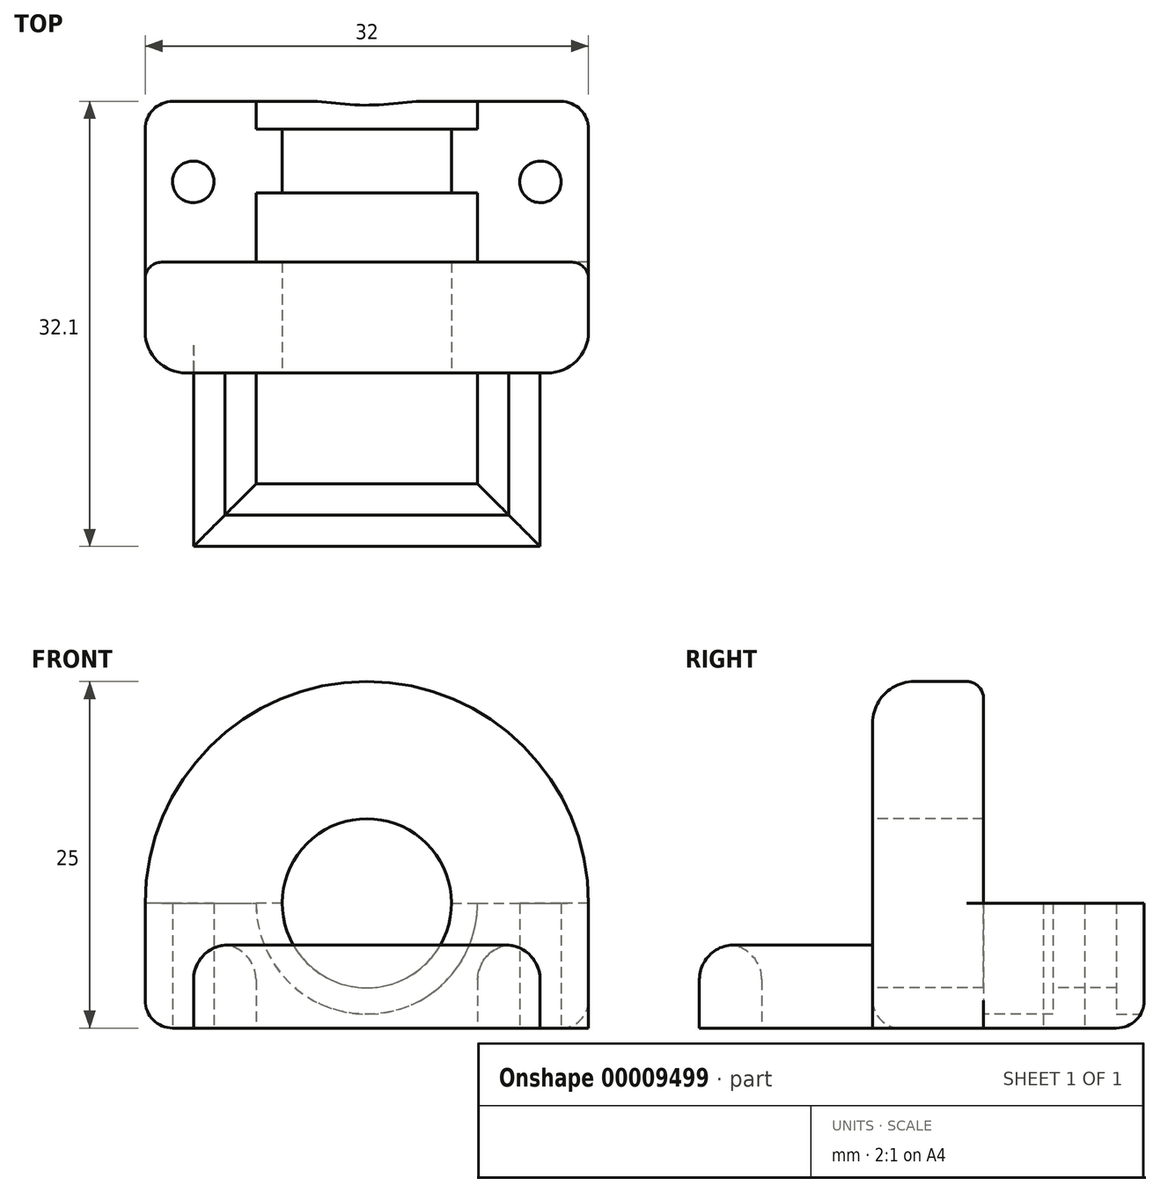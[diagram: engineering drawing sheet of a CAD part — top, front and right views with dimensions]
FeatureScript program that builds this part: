
annotation { "Feature Type Name" : "Feature", "Feature Type Description" : "" }
export const myFeature = defineFeature(function(context is Context, id is Id, definition is map)
    precondition{}
    {
        {
            var Q0;
            Q0=qCreatedBy(makeId("Top.planeOp"),FACE);
            var sketch = newSketch(context, id + "F0", { "sketchPlane" : qUnion([Q0])});
            skLineSegment(sketch, "E0.rect.bottom", {"start": v(-16, 5.8) * mm, "end": v(16, 5.8) * mm});
            skLineSegment(sketch, "E0.rect.top", {"start": v(-16, -5.8) * mm, "end": v(16, -5.8) * mm});
            skLineSegment(sketch, "E0.rect.left", {"start": v(-16, 5.8) * mm, "end": v(-16, -5.8) * mm});
            skLineSegment(sketch, "E0.rect.right", {"start": v(16, 5.8) * mm, "end": v(16, -5.8) * mm});
            skPoint(sketch, "E0.rect.middle", {"position": v(0, 0) * mm});
            skCircle(sketch, "E1", {"center": v(12.52, 0) * mm, "radius": 1.5 * mm});
            skCircle(sketch, "E2", {"center": v(-12.52, 0) * mm, "radius": 1.5 * mm});
            skSolve(sketch);
        }
        {
            var Q0;
            Q0=makeQuery(id+"F0.imprint","IMPRINT",FACE,{"disambiguationData":[TD([[makeQuery(id+"F0.imprint","IMPRINT",EDGE,{"derivedFrom":sQuery(id+"F0.wireOp",EDGE,"E0.rect.bottom")}),-1.0]])]});
            extrude(context, id + "F1", {"entities" : qUnion([Q0]), "depth" : 9 * mm});
        }
        {
            var Q0;
            Q0=makeQuery(id+"F1.opExtrude","SWEPT_FACE",FACE,{"disambiguationData":[OSD([sQuery(id+"F0.wireOp",EDGE,"E0.rect.top")])]});
            var sketch = newSketch(context, id + "F2", { "sketchPlane" : qUnion([Q0])});
            skCircle(sketch, "E3", {"center": v(0, 9) * mm, "radius": 8 * mm});
            skSolve(sketch);
        }
        {
            var Q0;
            Q0 = qSketchRegion(id + "F2", true);
            var Q1;
            Q1=makeQuery(id+"F1.opExtrude","SWEPT_FACE",FACE,{"disambiguationData":[OSD([sQuery(id+"F0.wireOp",EDGE,"E0.rect.bottom")])]});
            extrude(context, id + "F3", {"entities" : qUnion([Q0, Q1]), "operationType" : NewBodyOperationType.REMOVE, "oppositeDirection" : true, "depth" : 5 * mm});
        }
        {
            var Q0;
            Q0=makeQuery(id+"F1.opExtrude","SWEPT_FACE",FACE,{"disambiguationData":[OSD([sQuery(id+"F0.wireOp",EDGE,"E0.rect.bottom")])]});
            var sketch = newSketch(context, id + "F4", { "sketchPlane" : qUnion([Q0])});
            skCircle(sketch, "E4", {"center": v(0, 9) * mm, "radius": 8 * mm});
            skSolve(sketch);
        }
        {
            var Q0;
            Q0 = qSketchRegion(id + "F4", true);
            extrude(context, id + "F5", {"entities" : qUnion([Q0]), "operationType" : NewBodyOperationType.REMOVE, "oppositeDirection" : true, "depth" : 2 * mm});
        }
        {
            var Q0;
            Q0=makeQuery(id+"F5.boolean.opBoolean","COPY",FACE,{"derivedFrom":makeQuery(id+"F5.opExtrude","CAP_FACE",FACE,{"disambiguationData":[OSD([sQuery(id+"F4.wireOp",EDGE,"E4")])],"isStart":false})});
            var sketch = newSketch(context, id + "F6", { "sketchPlane" : qUnion([Q0])});
            skCircle(sketch, "E5", {"center": v(0, 9) * mm, "radius": 6 * mm});
            skSolve(sketch);
        }
        {
            var Q0;
            Q0 = qSketchRegion(id + "F6", true);
            extrude(context, id + "F7", {"entities" : qUnion([Q0]), "operationType" : NewBodyOperationType.REMOVE, "oppositeDirection" : true, "depth" : 25 * mm});
        }
        {
            var Q0;
            Q0=makeQuery(id+"F1.opExtrude","CAP_EDGE",EDGE,{"disambiguationData":[OSD([sQuery(id+"F0.wireOp",EDGE,"E0.rect.bottom")])],"isStart":true});
            var Q1;
            Q1=makeQuery(id+"F7.boolean.opBoolean","COPY",EDGE,{"derivedFrom":makeQuery(id+"F7.opExtrude","CAP_EDGE",EDGE,{"disambiguationData":[OSD([sQuery(id+"F6.wireOp",EDGE,"E5")])],"isStart":true})});
            var Q2;
            Q2=makeQuery(id+"F1.opExtrude","SWEPT_EDGE",EDGE,{"disambiguationData":[OSD([sQuery(id+"F0.wireOp",EDGE,"E0.rect.bottom"),sQuery(id+"F0.wireOp",EDGE,"E0.rect.left")])]});
            var Q3;
            Q3=makeQuery(id+"F1.opExtrude","CAP_EDGE",EDGE,{"disambiguationData":[OSD([sQuery(id+"F0.wireOp",EDGE,"E0.rect.left")])],"isStart":true});
            var Q4;
            Q4=makeQuery(id+"F1.opExtrude","CAP_EDGE",EDGE,{"disambiguationData":[OSD([sQuery(id+"F0.wireOp",EDGE,"E0.rect.right")])],"isStart":true});
            var Q5;
            Q5=makeQuery(id+"F1.opExtrude","SWEPT_EDGE",EDGE,{"disambiguationData":[OSD([sQuery(id+"F0.wireOp",EDGE,"E0.rect.bottom"),sQuery(id+"F0.wireOp",EDGE,"E0.rect.right")])]});
            fillet(context, id + "F8", {"entities" : qUnion([Q0, Q1, Q2, Q3, Q4, Q5]), "radius" : 2 * mm, "tangentPropagation" : true, "allowEdgeOverflow" : false});
        }
        {
            var Q0;
            Q0=makeQuery(id+"F1.opExtrude","SWEPT_FACE",FACE,{"disambiguationData":[OSD([sQuery(id+"F0.wireOp",EDGE,"E0.rect.top")])]});
            var sketch = newSketch(context, id + "F9", { "sketchPlane" : qUnion([Q0])});
            skArc(sketch, "E6", {"start": v(16, 9) * mm, "mid": v(0, 25) * mm, "end": v(-16, 9) * mm});
            skLineSegment(sketch, "E7", {"start": v(0, 0) * mm, "end": v(13.23, 0) * mm});
            skLineSegment(sketch, "E8", {"start": v(-13.23, 0) * mm, "end": v(0, 0) * mm});
            skLineSegment(sketch, "E9", {"start": v(-16, 9) * mm, "end": v(-16, 0) * mm});
            skLineSegment(sketch, "E10", {"start": v(16, 9) * mm, "end": v(16, 0) * mm});
            skLineSegment(sketch, "E11", {"start": v(-16, 0) * mm, "end": v(16, 0) * mm});
            skSolve(sketch);
        }
        {
            var Q0;
            Q0 = qSketchRegion(id + "F9", true);
            extrude(context, id + "F10", {"entities" : qUnion([Q0]), "operationType" : NewBodyOperationType.ADD, "depth" : 8 * mm});
        }
        {
            var Q0;
            Q0=qCreatedBy(makeId("Top.planeOp"),FACE);
            var sketch = newSketch(context, id + "F11", { "sketchPlane" : qUnion([Q0])});
            skLineSegment(sketch, "E12", {"start": v(-8, -13.8) * mm, "end": v(-12.5, -13.8) * mm});
            skLineSegment(sketch, "E13", {"start": v(-12.5, -13.8) * mm, "end": v(-8, -13.8) * mm});
            skLineSegment(sketch, "E14", {"start": v(12.5, -13.8) * mm, "end": v(12.5, -26.3) * mm});
            skLineSegment(sketch, "E15", {"start": v(12.5, -26.3) * mm, "end": v(-12.5, -26.3) * mm});
            skLineSegment(sketch, "E16", {"start": v(-12.5, -26.3) * mm, "end": v(-12.5, -13.8) * mm});
            skLineSegment(sketch, "E17", {"start": v(-8, -13.8) * mm, "end": v(-8, -21.8) * mm});
            skLineSegment(sketch, "E18", {"start": v(-8, -21.8) * mm, "end": v(8, -21.8) * mm});
            skLineSegment(sketch, "E19", {"start": v(8, -21.8) * mm, "end": v(8, -13.8) * mm});
            skLineSegment(sketch, "E20.trimOffspring", {"start": v(8, -13.8) * mm, "end": v(12.5, -13.8) * mm});
            skPoint(sketch, "E21.orphan", {"position": v(0, -13.8) * mm});
            skPoint(sketch, "E22", {"position": v(0, -21.8) * mm});
            skPoint(sketch, "E23", {"position": v(0, -26.3) * mm});
            skSolve(sketch);
        }
        {
            var Q0;
            Q0 = qSketchRegion(id + "F11", true);
            extrude(context, id + "F12", {"entities" : qUnion([Q0]), "operationType" : NewBodyOperationType.ADD, "depth" : 6 * mm});
        }
        {
            var Q0;
            Q0=makeQuery(id+"F12.opExtrude","CAP_EDGE",EDGE,{"disambiguationData":[OSD([sQuery(id+"F11.wireOp",EDGE,"E17")])],"isStart":false});
            var Q1;
            Q1=makeQuery(id+"F12.opExtrude","CAP_EDGE",EDGE,{"disambiguationData":[OSD([sQuery(id+"F11.wireOp",EDGE,"E16")])],"isStart":false});
            var Q2;
            Q2=makeQuery(id+"F12.opExtrude","CAP_EDGE",EDGE,{"disambiguationData":[OSD([sQuery(id+"F11.wireOp",EDGE,"E19")])],"isStart":false});
            var Q3;
            Q3=makeQuery(id+"F12.opExtrude","CAP_EDGE",EDGE,{"disambiguationData":[OSD([sQuery(id+"F11.wireOp",EDGE,"E14")])],"isStart":false});
            var Q4;
            Q4=makeQuery(id+"F12.opExtrude","CAP_EDGE",EDGE,{"disambiguationData":[OSD([sQuery(id+"F11.wireOp",EDGE,"E18")])],"isStart":false});
            var Q5;
            Q5=makeQuery(id+"F12.opExtrude","CAP_EDGE",EDGE,{"disambiguationData":[OSD([sQuery(id+"F11.wireOp",EDGE,"E15")])],"isStart":false});
            fillet(context, id + "F13", {"entities" : qUnion([Q0, Q1, Q2, Q3, Q4, Q5]), "radius" : 2.5 * mm, "tangentPropagation" : true, "allowEdgeOverflow" : false});
        }
        {
            var Q0;
            Q0=makeQuery(id+"F10.opExtrude","CAP_EDGE",EDGE,{"disambiguationData":[OSD([sQuery(id+"F9.wireOp",EDGE,"E6")])],"isStart":false});
            fillet(context, id + "F14", {"entities" : qUnion([Q0]), "radius" : 3 * mm, "tangentPropagation" : true, "allowEdgeOverflow" : false});
        }
        {
            var Q0;
            Q0=makeQuery(id+"F10.opExtrude","CAP_EDGE",EDGE,{"disambiguationData":[OSD([sQuery(id+"F9.wireOp",EDGE,"E6")])],"isStart":true});
            fillet(context, id + "F15", {"entities" : qUnion([Q0]), "radius" : 1.2 * mm, "tangentPropagation" : true, "allowEdgeOverflow" : false});
        }
        {
            var Q0;
            Q0=makeQuery(id+"F10.opExtrude","CAP_FACE",FACE,{"disambiguationData":[OSD([sQuery(id+"F9.wireOp",EDGE,"E6"),sQuery(id+"F9.wireOp",EDGE,"E9"),sQuery(id+"F9.wireOp",EDGE,"E10"),sQuery(id+"F9.wireOp",EDGE,"E11")])],"isStart":false});
            var sketch = newSketch(context, id + "F16", { "sketchPlane" : qUnion([Q0])});
            skCircle(sketch, "E24", {"center": v(0, 9) * mm, "radius": 6.1 * mm});
            skSolve(sketch);
        }
        {
            var Q0;
            Q0 = qSketchRegion(id + "F16", true);
            extrude(context, id + "F17", {"entities" : qUnion([Q0]), "operationType" : NewBodyOperationType.REMOVE, "flatOperationType" : FlatOperationType.REMOVE, "endBound" : BoundingType.THROUGH_ALL, "oppositeDirection" : true, "depth" : 25 * mm, "offsetDistance" : 25 * mm, "domain" : OperationDomain.MODEL});
        }
        {
            var Q0;
            Q0=makeQuery(id+"F14.opFillet","BLEND_EDGE",EDGE,{"blendedFrom":[makeQuery(id+"F10.opExtrude","CAP_EDGE",EDGE,{"disambiguationData":[OSD([sQuery(id+"F9.wireOp",EDGE,"E9")])],"isStart":false}),makeQuery(id+"F10.boolean.opBoolean","MERGE",FACE,{"derivedFrom":[makeQuery(id+"F1.opExtrude","CAP_FACE",FACE,{"disambiguationData":[OSD([sQuery(id+"F0.wireOp",EDGE,"E0.rect.bottom"),sQuery(id+"F0.wireOp",EDGE,"E0.rect.top"),sQuery(id+"F0.wireOp",EDGE,"E0.rect.left"),sQuery(id+"F0.wireOp",EDGE,"E0.rect.right"),sQuery(id+"F0.wireOp",EDGE,"E1"),sQuery(id+"F0.wireOp",EDGE,"E2")])],"isStart":true}),makeQuery(id+"F10.opExtrude","SWEPT_FACE",FACE,{"disambiguationData":[OSD([sQuery(id+"F9.wireOp",EDGE,"E11")])]})]})],"blendedInto":[makeQuery(id+"F10.boolean.opBoolean","MERGE",FACE,{"derivedFrom":[makeQuery(id+"F1.opExtrude","CAP_FACE",FACE,{"disambiguationData":[OSD([sQuery(id+"F0.wireOp",EDGE,"E0.rect.bottom"),sQuery(id+"F0.wireOp",EDGE,"E0.rect.top"),sQuery(id+"F0.wireOp",EDGE,"E0.rect.left"),sQuery(id+"F0.wireOp",EDGE,"E0.rect.right"),sQuery(id+"F0.wireOp",EDGE,"E1"),sQuery(id+"F0.wireOp",EDGE,"E2")])],"isStart":true}),makeQuery(id+"F10.opExtrude","SWEPT_FACE",FACE,{"disambiguationData":[OSD([sQuery(id+"F9.wireOp",EDGE,"E11")])]})]})]});
            fillet(context, id + "F18", {"entities" : qUnion([Q0]), "radius" : 2 * mm, "tangentPropagation" : true, "allowEdgeOverflow" : false});
        }
    });
